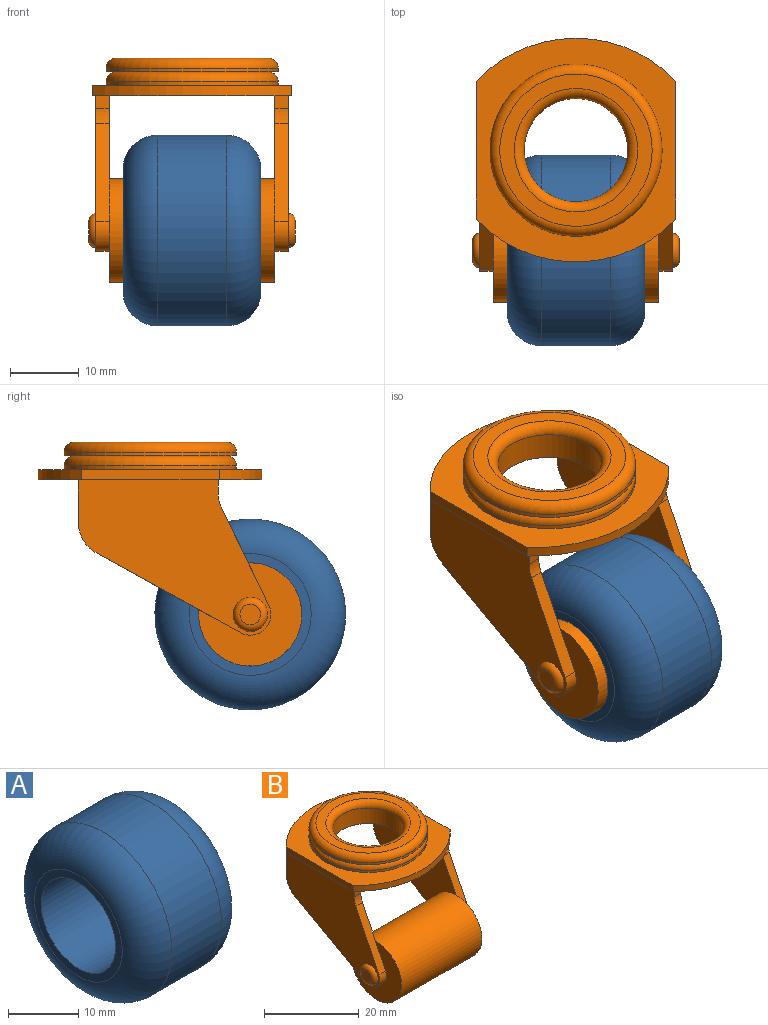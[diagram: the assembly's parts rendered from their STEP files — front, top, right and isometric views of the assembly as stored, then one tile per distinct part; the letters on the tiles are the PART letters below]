
ASSEMBLY  parts=2 mates=1
PART A: 6 faces, bbox 20x30x30 mm
  f0: cylinder r=7.49mm len=20mm, axis (-1,0,0), area 941.3mm2, adj f2,f3
  f1: cylinder r=13.84mm len=27.68mm, axis (-1,0,0), area 869.6mm2, adj f4,f5
  f2: plane 17.68x17.68mm, normal (1,0,0), area 69.3mm2, adj f0,f5
  f3: plane 17.68x17.68mm, normal (-1,0,0), area 69.3mm2, adj f0,f4
  f4: torus R=8.84mm, axis (1,0,0), area 593.3mm2, adj f1,f3
  f5: torus R=8.84mm, axis (1,0,0), area 593.3mm2, adj f1,f2
PART B: 39 faces, bbox 30x38.2x32.5 mm
  f0: plane 24.67x18.84mm, normal (1,0,0), area 308.9mm2, adj f3,f4,f8,f11,f12,f17,f33,f34
  f1: plane 24.67x18.84mm, normal (-1,0,0), area 308.9mm2, adj f6,f7,f8,f14,f15,f17,f31,f32
  f2: plane 27.95x22.54mm, normal (-1,0,0), area 361.7mm2, adj f3,f4,f11,f12,f13,f17,f33,f34
  f3: plane 2x1.8mm, normal (0,-1,0), area 3.6mm2, adj f0,f2,f17,f34
  f4: plane 6.22x2mm, normal (0,1,0), area 12.4mm2, adj f0,f2,f17,f33
  f5: plane 27.95x22.54mm, normal (1,0,0), area 361.7mm2, adj f6,f7,f14,f15,f16,f17,f31,f32
  f6: plane 2x1.8mm, normal (0,-1,0), area 3.6mm2, adj f1,f5,f17,f32
  f7: plane 6.22x2mm, normal (0,1,0), area 12.4mm2, adj f1,f5,f17,f31
  f8: cylinder r=7.49mm len=24mm, axis (-1,0,0), area 1129.5mm2, adj f0,f1,f9,f10
  f9: plane 14.98x14.98mm, normal (1,0,0), area 103.9mm2, adj f8,f14,f15,f16
  f10: plane 14.98x14.98mm, normal (-1,0,0), area 103.9mm2, adj f8,f11,f12,f13
  f11: plane 14.27x6.89mm, normal (0,-0.9,0.43), area 31.7mm2, adj f0,f2,f10,f13,f34
  f12: plane 20.91x11.57mm, normal (0,0.48,-0.87), area 47.8mm2, adj f0,f2,f10,f13,f33
  f13: cylinder r=3mm len=4.45mm, axis (1,0,0), area 15.2mm2, adj f2,f10,f11,f12
  f14: plane 14.27x6.89mm, normal (0,-0.9,0.43), area 31.7mm2, adj f1,f5,f9,f16,f32
  f15: plane 20.91x11.57mm, normal (0,0.48,-0.87), area 47.8mm2, adj f1,f5,f9,f16,f31
  f16: cylinder r=3mm len=4.45mm, axis (-1,0,0), area 15.2mm2, adj f5,f9,f14,f15
  f17: plane 32.45x29mm, normal (0,0,-1), area 571.6mm2, adj f0,f1,f2,f3,f4,f5,f6,f7
  f18: cylinder r=19.97mm len=29mm, axis (0,0,-1), area 47.4mm2, adj f17,f19,f21,f22
  f19: plane 20x1.46mm, normal (-1,0,0), area 29.2mm2, adj f17,f18,f20,f22
  f20: cylinder r=20.03mm len=29mm, axis (0,0,-1), area 47.3mm2, adj f17,f19,f21,f22
  f21: plane 20x1.46mm, normal (1,0,0), area 29.2mm2, adj f17,f18,f20,f22
  f22: plane 32.45x29mm, normal (0,0,1), area 338.5mm2, adj f18,f19,f20,f21,f24
  f23: cylinder r=7.5mm len=15mm, axis (0,0,-1), area 189mm2, adj f17,f29
  f24: cylinder r=12.5mm len=25mm, axis (0,0,-1), area 43.3mm2, adj f22,f25
  f25: torus R=11.05mm, axis (0,0,1), area 171.2mm2, adj f24,f28
  f26: cylinder r=12.5mm len=25mm, axis (0,0,-1), area 43.3mm2, adj f28,f30
  f27: plane 22.1x22.1mm, normal (0,0,1), area 132.1mm2, adj f29,f30
  f28: plane 25x25mm, normal (0,0,-1), area 107.2mm2, adj f25,f26
  f29: torus R=8.95mm, axis (0,0,1), area 114.7mm2, adj f23,f27
  f30: torus R=11.05mm, axis (0,0,1), area 171.2mm2, adj f26,f27
  f31: cylinder r=5mm len=4.38mm, axis (-1,0,0), area 10.7mm2, adj f1,f5,f7,f15
  f32: cylinder r=5mm len=2.17mm, axis (1,0,0), area 4.5mm2, adj f1,f5,f6,f14
  f33: cylinder r=5mm len=4.38mm, axis (1,0,0), area 10.7mm2, adj f0,f2,f4,f12
  f34: cylinder r=5mm len=2.17mm, axis (-1,0,0), area 4.5mm2, adj f0,f2,f3,f11
  f35: plane 2.98x2.98mm, normal (1,0,0), area 7mm2, adj f38
  f36: plane 2.98x2.98mm, normal (-1,0,0), area 7mm2, adj f37
  f37: torus R=1.49mm, axis (1,0,0), area 21mm2, adj f2,f36
  f38: torus R=1.49mm, axis (1,0,0), area 21mm2, adj f5,f35
PLACE A t=(0,-14.5,-25)mm
PLACE B t=(0,-14.5,-25)mm
MATE fastened A.f0 <-> B.f13  axis (1,0,0) through (10,-14.5,-25)mm
